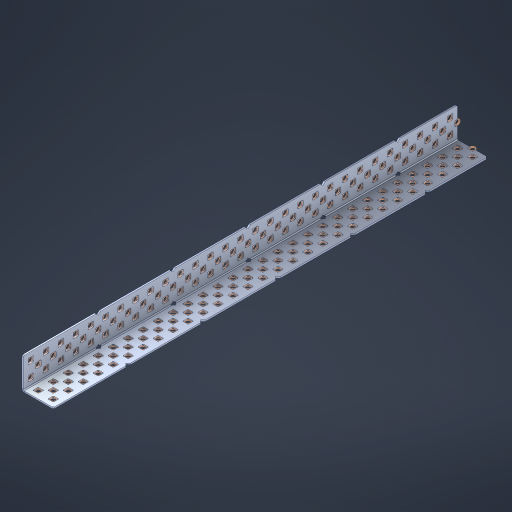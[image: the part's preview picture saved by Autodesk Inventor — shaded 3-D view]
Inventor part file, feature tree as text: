
AUTODESK INVENTOR PART (.ipt)
format: ipt  version: 2023 (Build 270158000, 158)  size: 2,015,744 bytes
history: native  units: in
note: dims shown in document units (in); Inventor stores cm internally (conversion verified against a paired STEP export)
features: other x180, extrude x172, sheet_metal_op x8, sketch x7, pattern_linear x2, mirror x1, chamfer x1
ambient origin geometry x8: Origin, YZ Plane, XZ Plane, XY Plane, X Axis, Y Axis, Z Axis, Center Point
bodies: Solid1 (feature_tree), Body (feature_tree)
feature tree (371):
  sheet_metal_op  "Flanges"
  sheet_metal_op  "Body Pattern"
  pattern_linear  "Center Pattern"  Spacing1=1.0in  [1 undecoded]
  other  "Arc Length"
  pattern_linear  "Notch Pattern"  Spacing1=0.1875in  [1 undecoded]
  other  "Diagonal Plane"
  mirror  "Everything Mirrored"
  chamfer  "End Chamfer"
  sketch  "Sketch1"  dims[d0=1.0in]
  other  "Plate1"
  sketch  "Sketch2"  dims[d1=14.5in]
  other  "Plate2"
  sheet_metal_op  "Bend1"
  sheet_metal_op  "Corner1"
  sketch  "Sketch8"  dims[d2=0.0469in]
  sketch  "Sketch9"  dims[d3=0.0469in]
  other  "Srf91"
  sheet_metal_op  "Body Pattern Sketch"
  other  "Srf92"
  sketch  "Sketch13"  dims[d4=0.0234in]
  sketch  "Sketch15"  dims[d5=0.0938in]
  sketch  "Sketch16"  dims[d6=0.0469in d7=1.0in d8=90.0deg d9=0.0312in d10=0.1875in d11=0.0469in d12=0.0469in d49=0.182in d50=0.02in d52=0.25in d53=0.0469in d54=0.0in d55=0.172in d56=1.0in d57=0.0in d60=11.4173in d62=0.5in d63=0.7874in d65=0.5in d85=0.1473in d86=0.1659in d89=0.0469in d90=0.0in d91=0.04in d92=0.0491in d95=2.5in d96=0.04in d97=0.25in d98=45.0deg d99=0.25in d106=0.182in d107=0.02in d108=0.5in d110=0.0469in d111=0.0in d112=0.172in d113=0.5in d114=0.0in d117=0.5in d123=0.25in d125=0.25in d126=0.0491in d127=0.1227in d128=0.08in d129=0.04in d130=2.5in]
  other  "Srf786"
  other  "Srf856"
  other  "Srf857"
  other  "Srf858"
  other  "Srf859"
  other  "Srf860"
  other  "Srf861"
  other  "Srf889"
  other  "Srf890"
  other  "Srf891"
  other  "Srf1275"
  other  "Srf1276"
  other  "Srf1278"
  other  "Srf1279"
  other  "Srf1280"
  other  "Srf1281"
  other  "Srf1282"
  other  "Srf1283"
  other  "Srf1277"
  other  "Srf1285"
  other  "Srf1286"
  other  "Srf1287"
  other  "Srf1383"
  other  "Srf1384"
  other  "Srf1385"
  other  "Srf1386"
  other  "Srf1387"
  other  "Srf1388"
  other  "Srf1389"
  other  "Srf1390"
  other  "Srf1391"
  other  "Srf1392"
  other  "Srf1393"
  other  "Srf1394"
  other  "Srf1395"
  other  "Srf1396"
  other  "Srf1397"
  other  "Srf1398"
  other  "Srf1399"
  other  "Srf1400"
  other  "Srf1401"
  other  "Srf1402"
  other  "Srf1403"
  other  "Srf1404"
  other  "Srf1405"
  other  "Srf1406"
  other  "Srf1407"
  other  "Srf1408"
  other  "Srf1409"
  other  "Srf1410"
  other  "Srf1411"
  other  "Srf1412"
  other  "Srf1413"
  other  "Srf1414"
  other  "Srf1415"
  other  "Srf1416"
  other  "Srf1417"
  other  "Srf1418"
  other  "Srf1419"
  other  "Srf1420"
  other  "Srf1421"
  other  "Srf1422"
  other  "Srf1423"
  other  "Srf1424"
  other  "Srf1425"
  other  "Srf1426"
  other  "Srf1427"
  other  "Srf1428"
  other  "Srf1429"
  other  "Srf1430"
  other  "Srf1431"
  other  "Srf1432"
  other  "Srf1445"
  other  "Srf1446"
  other  "Srf1447"
  other  "Srf1448"
  other  "Srf1449"
  other  "Srf1450"
  other  "Srf1451"
  other  "Srf1452"
  other  "Srf1453"
  other  "Srf1454"
  other  "Srf1455"
  other  "Srf1456"
  other  "Srf1457"
  other  "Srf1458"
  other  "Srf1459"
  other  "Srf1460"
  other  "Srf1461"
  other  "Srf1462"
  other  "Srf1463"
  other  "Srf1464"
  other  "Srf1465"
  other  "Srf1466"
  other  "Srf1467"
  other  "Srf1468"
  other  "Srf1469"
  other  "Srf1475"
  other  "Srf1476"
  other  "Srf1477"
  other  "Srf1478"
  other  "Srf1479"
  other  "Srf1480"
  other  "Srf1481"
  other  "Srf1482"
  other  "Srf1483"
  other  "Srf1484"
  other  "Srf1485"
  other  "Srf1486"
  other  "Srf1487"
  other  "Srf1488"
  other  "Srf1489"
  other  "Srf1490"
  other  "Srf1491"
  other  "Srf1492"
  other  "Srf1493"
  other  "Srf1494"
  other  "Srf1495"
  other  "Srf1496"
  other  "Srf1497"
  other  "Srf1498"
  other  "Srf1499"
  other  "Srf1500"
  other  "Srf1501"
  other  "Srf1502"
  other  "Srf1503"
  other  "Srf1504"
  other  "Srf1505"
  other  "Srf1506"
  other  "Srf1507"
  other  "Srf1508"
  other  "Srf1509"
  other  "Srf1510"
  other  "Srf1511"
  other  "Srf1512"
  other  "Srf1513"
  other  "Srf1514"
  other  "Srf1515"
  other  "Srf1516"
  other  "Srf1517"
  other  "Srf1518"
  other  "Srf1519"
  other  "Srf1520"
  other  "Srf1521"
  other  "Srf1522"
  other  "Srf1523"
  other  "Srf1524"
  other  "Srf1537"
  other  "Srf1538"
  other  "Srf1539"
  other  "Srf1540"
  other  "Srf1541"
  other  "Srf1542"
  other  "Srf1543"
  other  "Srf1544"
  other  "Srf1545"
  other  "Srf1546"
  other  "Srf1547"
  other  "Srf1548"
  other  "Srf1549"
  other  "Srf1550"
  other  "Srf1551"
  other  "Srf1552"
  other  "Srf1553"
  other  "Srf1554"
  other  "Srf1555"
  other  "Srf1556"
  other  "Srf1557"
  other  "Srf1558"
  other  "Srf1559"
  other  "Srf1560"
  other  "Srf1561"
  sheet_metal_op  "Body Stamp"
  sheet_metal_op  "Body Circle"
  other  "Center Stamp"
  other  "Center Circle"
  sheet_metal_op  "Notch"
  extrude  "ExtrusionSrf92"  Depth=0.0469in
  extrude  "ExtrusionSrf856"  Depth=0.0469in
  extrude  "ExtrusionSrf857"  Depth=0.182in
  extrude  "ExtrusionSrf858"  Depth=0.02in
  extrude  "ExtrusionSrf859"  Depth=0.25in
  extrude  "ExtrusionSrf860"  Depth=0.0469in
  extrude  "ExtrusionSrf861"  TaperAngle=0.0deg  [1 undecoded]
  extrude  "ExtrusionSrf889"  Depth=2.5in
  extrude  "ExtrusionSrf890"  Depth=1.0in TaperAngle=0.0deg
  extrude  "ExtrusionSrf891"  Depth=2.5in
  extrude  "ExtrusionSrf1275"  Depth=0.5in
  extrude  "ExtrusionSrf1276"  Depth=2.5in
  extrude  "ExtrusionSrf1277"  Depth=2.5in
  extrude  "ExtrusionSrf1278"  Depth=0.0469in
  extrude  "ExtrusionSrf1279"  Depth=2.5in TaperAngle=0.0deg
  extrude  "ExtrusionSrf1280"  Depth=2.5in
  extrude  "ExtrusionSrf1281"  Depth=0.25in TaperAngle=45.0deg
  extrude  "ExtrusionSrf1282"  Depth=0.25in
  extrude  "ExtrusionSrf1345"  Depth=0.182in
  extrude  "ExtrusionSrf1346"  Depth=0.02in
  extrude  "ExtrusionSrf1347"  Depth=0.5in
  extrude  "ExtrusionSrf1348"  Depth=0.0469in
  extrude  "ExtrusionSrf1383"  TaperAngle=0.0deg  [1 undecoded]
  extrude  "ExtrusionSrf1384"  Depth=2.5in
  extrude  "ExtrusionSrf1385"  Depth=0.5in TaperAngle=0.0deg
  extrude  "ExtrusionSrf1386"  Depth=0.5in
  extrude  "ExtrusionSrf1387"  Depth=0.25in
  extrude  "ExtrusionSrf1388"  Depth=0.25in
  extrude  "ExtrusionSrf1389"  Depth=2.5in
  extrude  "ExtrusionSrf1390"  Depth=2.5in
  extrude  "ExtrusionSrf1391"  Depth=2.5in
  extrude  "ExtrusionSrf1392"  Depth=2.5in
  extrude  "ExtrusionSrf1393"  Depth=2.5in
  extrude  "ExtrusionSrf1394"  [1 undecoded]
  extrude  "ExtrusionSrf1395"  [1 undecoded]
  extrude  "ExtrusionSrf1396"  [1 undecoded]
  extrude  "ExtrusionSrf1397"  [1 undecoded]
  extrude  "ExtrusionSrf1398"  [1 undecoded]
  extrude  "ExtrusionSrf1399"  [1 undecoded]
  extrude  "ExtrusionSrf1400"  [1 undecoded]
  extrude  "ExtrusionSrf1401"  [1 undecoded]
  extrude  "ExtrusionSrf1402"  [1 undecoded]
  extrude  "ExtrusionSrf1403"  [1 undecoded]
  extrude  "ExtrusionSrf1404"  [1 undecoded]
  extrude  "ExtrusionSrf1405"  [1 undecoded]
  extrude  "ExtrusionSrf1406"  [1 undecoded]
  extrude  "ExtrusionSrf1407"  [1 undecoded]
  extrude  "ExtrusionSrf1408"  [1 undecoded]
  extrude  "ExtrusionSrf1409"  [1 undecoded]
  extrude  "ExtrusionSrf1410"  [1 undecoded]
  extrude  "ExtrusionSrf1411"  [1 undecoded]
  extrude  "ExtrusionSrf1412"  [1 undecoded]
  extrude  "ExtrusionSrf1413"  [1 undecoded]
  extrude  "ExtrusionSrf1414"  [1 undecoded]
  extrude  "ExtrusionSrf1415"  [1 undecoded]
  extrude  "ExtrusionSrf1416"  [1 undecoded]
  extrude  "ExtrusionSrf1417"  [1 undecoded]
  extrude  "ExtrusionSrf1418"  [1 undecoded]
  extrude  "ExtrusionSrf1419"  [1 undecoded]
  extrude  "ExtrusionSrf1420"  [1 undecoded]
  extrude  "ExtrusionSrf1421"  [1 undecoded]
  extrude  "ExtrusionSrf1422"  [1 undecoded]
  extrude  "ExtrusionSrf1423"  [1 undecoded]
  extrude  "ExtrusionSrf1424"  [1 undecoded]
  extrude  "ExtrusionSrf1425"  [1 undecoded]
  extrude  "ExtrusionSrf1426"  [1 undecoded]
  extrude  "ExtrusionSrf1427"  [1 undecoded]
  extrude  "ExtrusionSrf1428"  [1 undecoded]
  extrude  "ExtrusionSrf1429"  [1 undecoded]
  extrude  "ExtrusionSrf1430"  [1 undecoded]
  extrude  "ExtrusionSrf1431"  [1 undecoded]
  extrude  "ExtrusionSrf1432"  [1 undecoded]
  extrude  "ExtrusionSrf1445"  [1 undecoded]
  extrude  "ExtrusionSrf1446"  [1 undecoded]
  extrude  "ExtrusionSrf1447"  [1 undecoded]
  extrude  "ExtrusionSrf1448"  [1 undecoded]
  extrude  "ExtrusionSrf1449"  [1 undecoded]
  extrude  "ExtrusionSrf1450"  [1 undecoded]
  extrude  "ExtrusionSrf1451"  [1 undecoded]
  extrude  "ExtrusionSrf1452"  [1 undecoded]
  extrude  "ExtrusionSrf1453"  [1 undecoded]
  extrude  "ExtrusionSrf1454"  [1 undecoded]
  extrude  "ExtrusionSrf1455"  [1 undecoded]
  extrude  "ExtrusionSrf1456"  [1 undecoded]
  extrude  "ExtrusionSrf1457"  [1 undecoded]
  extrude  "ExtrusionSrf1458"  [1 undecoded]
  extrude  "ExtrusionSrf1459"  [1 undecoded]
  extrude  "ExtrusionSrf1460"  [1 undecoded]
  extrude  "ExtrusionSrf1461"  [1 undecoded]
  extrude  "ExtrusionSrf1462"  [1 undecoded]
  extrude  "ExtrusionSrf1463"  [1 undecoded]
  extrude  "ExtrusionSrf1464"  [1 undecoded]
  extrude  "ExtrusionSrf1465"  [1 undecoded]
  extrude  "ExtrusionSrf1466"  [1 undecoded]
  extrude  "ExtrusionSrf1467"  [1 undecoded]
  extrude  "ExtrusionSrf1468"  [1 undecoded]
  extrude  "ExtrusionSrf1469"  [1 undecoded]
  extrude  "ExtrusionSrf1475"  [1 undecoded]
  extrude  "ExtrusionSrf1476"  [1 undecoded]
  extrude  "ExtrusionSrf1477"  [1 undecoded]
  extrude  "ExtrusionSrf1478"  [1 undecoded]
  extrude  "ExtrusionSrf1479"  [1 undecoded]
  extrude  "ExtrusionSrf1480"  [1 undecoded]
  extrude  "ExtrusionSrf1481"  [1 undecoded]
  extrude  "ExtrusionSrf1482"  [1 undecoded]
  extrude  "ExtrusionSrf1483"  [1 undecoded]
  extrude  "ExtrusionSrf1484"  [1 undecoded]
  extrude  "ExtrusionSrf1485"  [1 undecoded]
  extrude  "ExtrusionSrf1486"  [1 undecoded]
  extrude  "ExtrusionSrf1487"  [1 undecoded]
  extrude  "ExtrusionSrf1488"  [1 undecoded]
  extrude  "ExtrusionSrf1489"  [1 undecoded]
  extrude  "ExtrusionSrf1490"  [1 undecoded]
  extrude  "ExtrusionSrf1491"  [1 undecoded]
  extrude  "ExtrusionSrf1492"  [1 undecoded]
  extrude  "ExtrusionSrf1493"  [1 undecoded]
  extrude  "ExtrusionSrf1494"  [1 undecoded]
  extrude  "ExtrusionSrf1495"  [1 undecoded]
  extrude  "ExtrusionSrf1496"  [1 undecoded]
  extrude  "ExtrusionSrf1497"  [1 undecoded]
  extrude  "ExtrusionSrf1498"  [1 undecoded]
  extrude  "ExtrusionSrf1499"  [1 undecoded]
  extrude  "ExtrusionSrf1500"  [1 undecoded]
  extrude  "ExtrusionSrf1501"  [1 undecoded]
  extrude  "ExtrusionSrf1502"  [1 undecoded]
  extrude  "ExtrusionSrf1503"  [1 undecoded]
  extrude  "ExtrusionSrf1504"  [1 undecoded]
  extrude  "ExtrusionSrf1505"  [1 undecoded]
  extrude  "ExtrusionSrf1506"  [1 undecoded]
  extrude  "ExtrusionSrf1507"  [1 undecoded]
  extrude  "ExtrusionSrf1508"  [1 undecoded]
  extrude  "ExtrusionSrf1509"  [1 undecoded]
  extrude  "ExtrusionSrf1510"  [1 undecoded]
  extrude  "ExtrusionSrf1511"  [1 undecoded]
  extrude  "ExtrusionSrf1512"  [1 undecoded]
  extrude  "ExtrusionSrf1513"  [1 undecoded]
  extrude  "ExtrusionSrf1514"  [1 undecoded]
  extrude  "ExtrusionSrf1515"  [1 undecoded]
  extrude  "ExtrusionSrf1516"  [1 undecoded]
  extrude  "ExtrusionSrf1517"  [1 undecoded]
  extrude  "ExtrusionSrf1518"  [1 undecoded]
  extrude  "ExtrusionSrf1519"  [1 undecoded]
  extrude  "ExtrusionSrf1520"  [1 undecoded]
  extrude  "ExtrusionSrf1521"  [1 undecoded]
  extrude  "ExtrusionSrf1522"  [1 undecoded]
  extrude  "ExtrusionSrf1523"  [1 undecoded]
  extrude  "ExtrusionSrf1524"  [1 undecoded]
  extrude  "ExtrusionSrf1537"  [1 undecoded]
  extrude  "ExtrusionSrf1538"  [1 undecoded]
  extrude  "ExtrusionSrf1539"  [1 undecoded]
  extrude  "ExtrusionSrf1540"  [1 undecoded]
  extrude  "ExtrusionSrf1541"  [1 undecoded]
  extrude  "ExtrusionSrf1542"  [1 undecoded]
  extrude  "ExtrusionSrf1543"  [1 undecoded]
  extrude  "ExtrusionSrf1544"  [1 undecoded]
  extrude  "ExtrusionSrf1545"  [1 undecoded]
  extrude  "ExtrusionSrf1546"  [1 undecoded]
  extrude  "ExtrusionSrf1547"  [1 undecoded]
  extrude  "ExtrusionSrf1548"  [1 undecoded]
  extrude  "ExtrusionSrf1549"  [1 undecoded]
  extrude  "ExtrusionSrf1550"  [1 undecoded]
  extrude  "ExtrusionSrf1551"  [1 undecoded]
  extrude  "ExtrusionSrf1552"  [1 undecoded]
  extrude  "ExtrusionSrf1553"  [1 undecoded]
  extrude  "ExtrusionSrf1554"  [1 undecoded]
  extrude  "ExtrusionSrf1555"  [1 undecoded]
  extrude  "ExtrusionSrf1556"  [1 undecoded]
  extrude  "ExtrusionSrf1557"  [1 undecoded]
  extrude  "ExtrusionSrf1558"  [1 undecoded]
  extrude  "ExtrusionSrf1559"  [1 undecoded]
  extrude  "ExtrusionSrf1560"  [1 undecoded]
  extrude  "ExtrusionSrf1561"  [1 undecoded]
note: 143 required parameter values undecoded (feature->parameter linkage not recoverable at this tier; creation-order binding heuristic only, values carry confidence <= 0.55)
